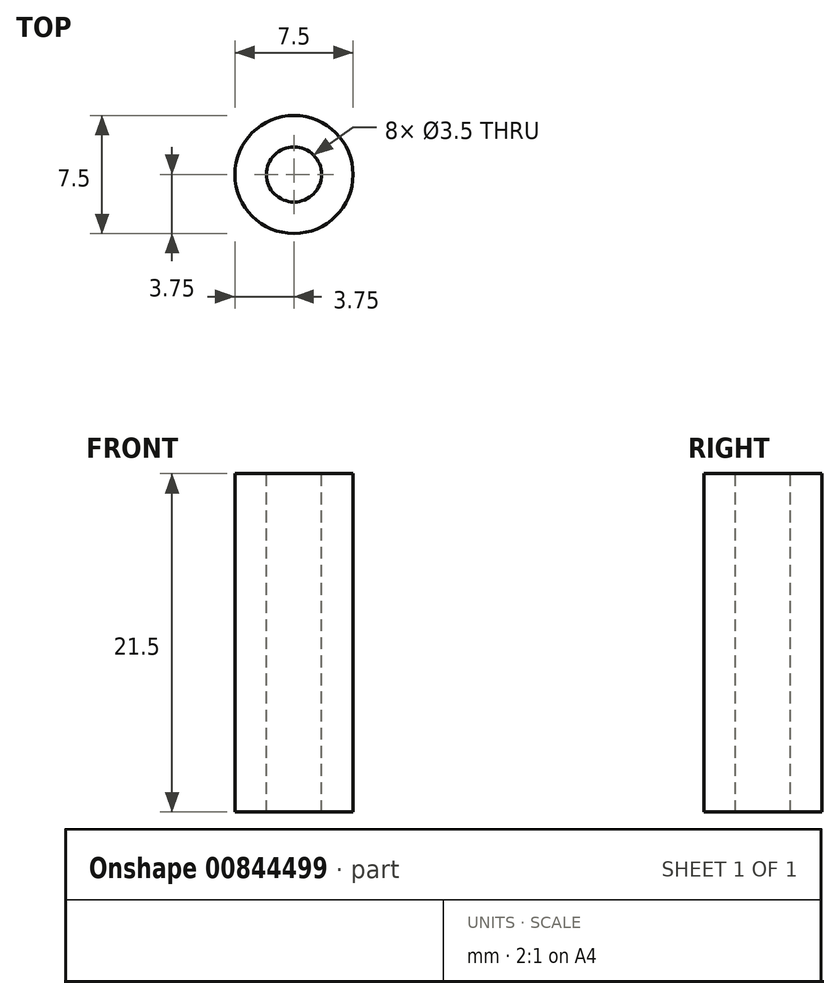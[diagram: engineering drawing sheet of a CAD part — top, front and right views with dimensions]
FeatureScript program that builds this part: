
annotation { "Feature Type Name" : "Feature", "Feature Type Description" : "" }
export const myFeature = defineFeature(function(context is Context, id is Id, definition is map)
    precondition{}
    {
        {
            var Q0;
            Q0=qCreatedBy(makeId("Top.planeOp"),FACE);
            var sketch = newSketch(context, id + "F0", { "sketchPlane" : qUnion([Q0])});
            skCircle(sketch, "E0", {"center": v(0, 0) * mm, "radius": 1.75 * mm});
            skLineSegment(sketch, "E1", {"start": v(0, 2.78) * mm, "end": v(0, -4.67) * mm, "construction": true});
            skLineSegment(sketch, "E2", {"start": v(-1.75, 0) * mm, "end": v(1.75, 0) * mm, "construction": true});
            skCircle(sketch, "E3.0", {"center": v(0, 0) * mm, "radius": 3.75 * mm});
            skSolve(sketch);
        }
        {
            var Q0;
            Q0=makeQuery(id+"F0.imprint","IMPRINT",FACE,{"disambiguationData":[TD([[makeQuery(id+"F0.imprint","IMPRINT",EDGE,{"derivedFrom":sQuery(id+"F0.wireOp",EDGE,"E0")}),-1.0]])]});
            extrude(context, id + "F1", {"entities" : qUnion([Q0]), "oppositeDirection" : true, "depth" : 21.5 * mm, "offsetDistance" : 25 * mm});
        }
    });
